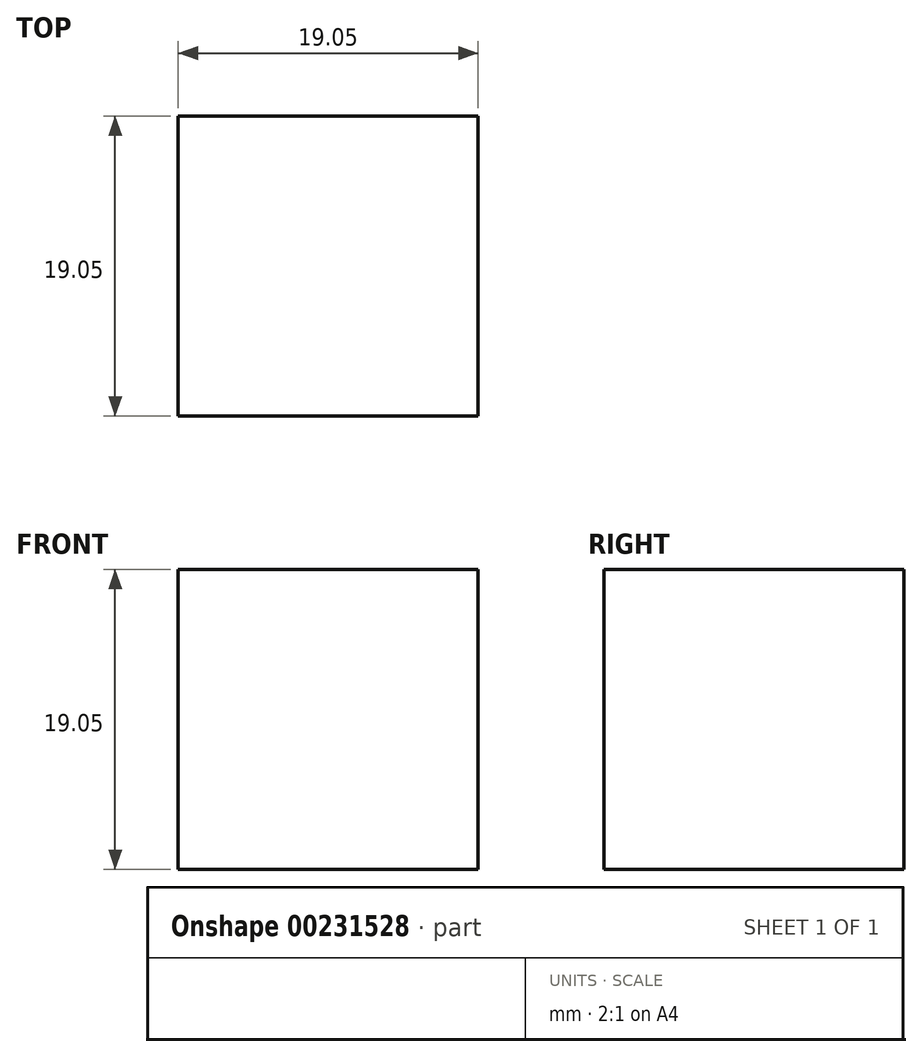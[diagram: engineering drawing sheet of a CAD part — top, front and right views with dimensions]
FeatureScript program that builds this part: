
annotation { "Feature Type Name" : "Feature", "Feature Type Description" : "" }
export const myFeature = defineFeature(function(context is Context, id is Id, definition is map)
    precondition{}
    {
        {
            var Q0;
            Q0=qCreatedBy(makeId("Front.planeOp"),FACE);
            var sketch = newSketch(context, id + "F0", { "sketchPlane" : qUnion([Q0])});
            skLineSegment(sketch, "E0.bottom", {"start": v(-10.1, 5.81) * mm, "end": v(8.95, 5.81) * mm});
            skLineSegment(sketch, "E0.top", {"start": v(-10.1, -13.24) * mm, "end": v(8.95, -13.24) * mm});
            skLineSegment(sketch, "E0.left", {"start": v(-10.1, 5.81) * mm, "end": v(-10.1, -13.24) * mm});
            skLineSegment(sketch, "E0.right", {"start": v(8.95, 5.81) * mm, "end": v(8.95, -13.24) * mm});
            skSolve(sketch);
        }
        {
            var Q0;
            Q0 = qSketchRegion(id + "F0", true);
            extrude(context, id + "F1", {"entities" : qUnion([Q0]), "depth" : 19.05 * mm});
        }
    });
